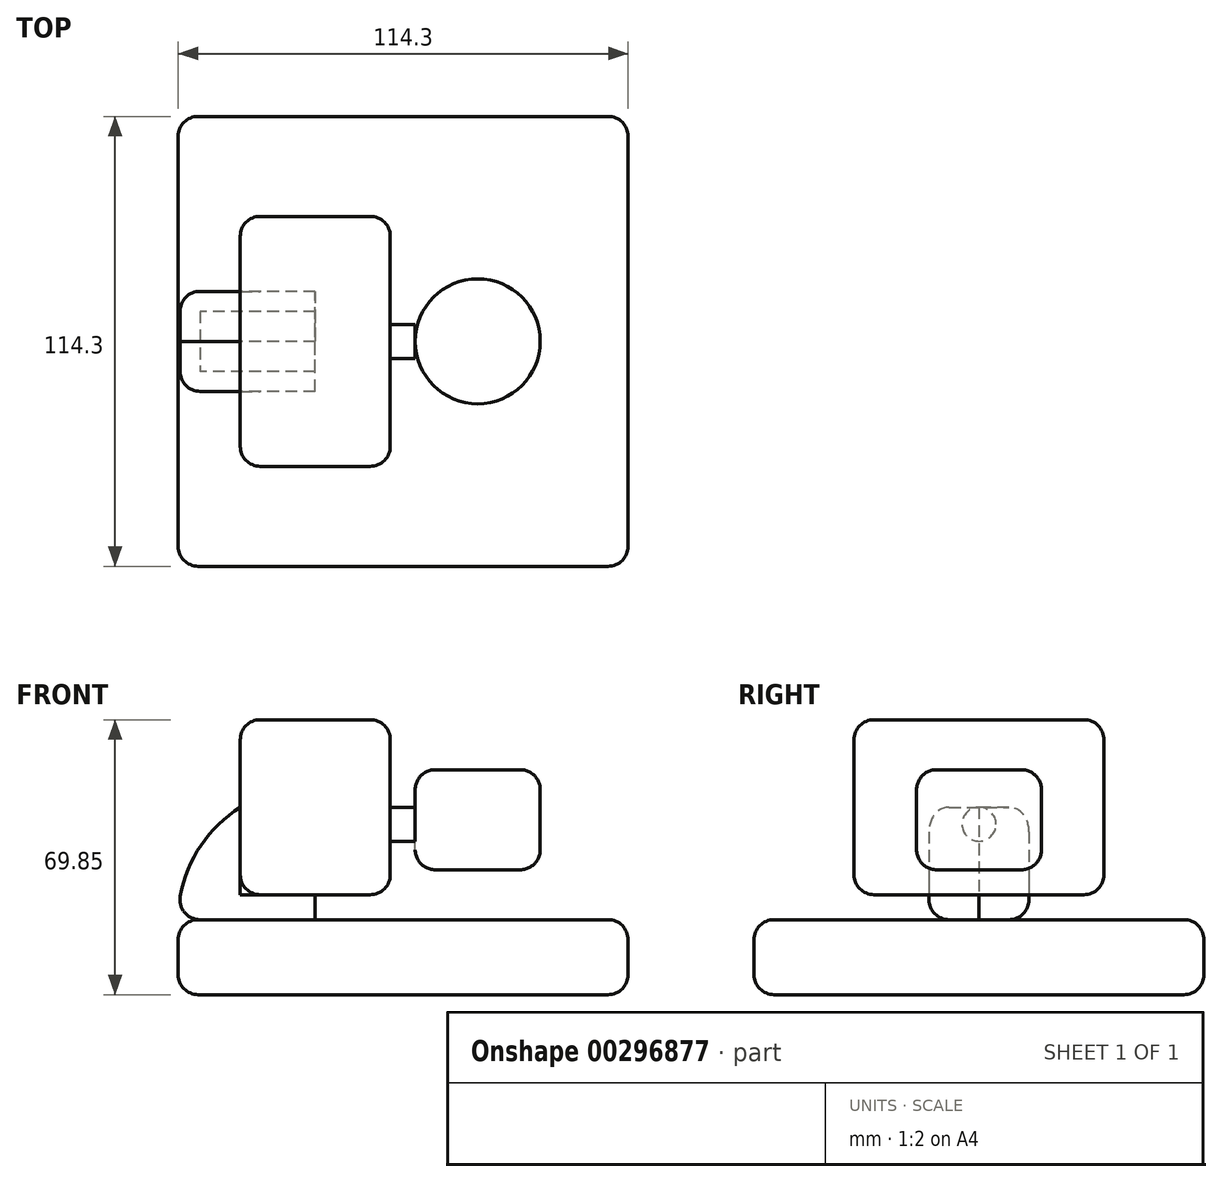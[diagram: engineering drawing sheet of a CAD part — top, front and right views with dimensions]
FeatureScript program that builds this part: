
annotation { "Feature Type Name" : "Feature", "Feature Type Description" : "" }
export const myFeature = defineFeature(function(context is Context, id is Id, definition is map)
    precondition{}
    {
        {
            var Q0;
            Q0=qCreatedBy(makeId("Front.planeOp"),FACE);
            var sketch = newSketch(context, id + "F0", { "sketchPlane" : qUnion([Q0])});
            skLineSegment(sketch, "E0.bottom", {"start": v(57.15, -38.1) * mm, "end": v(-57.15, -38.1) * mm});
            skLineSegment(sketch, "E0.top", {"start": v(57.15, -57.15) * mm, "end": v(-57.15, -57.15) * mm});
            skLineSegment(sketch, "E0.left", {"start": v(57.15, -38.1) * mm, "end": v(57.15, -57.15) * mm});
            skLineSegment(sketch, "E0.right", {"start": v(-57.15, -38.1) * mm, "end": v(-57.15, -57.15) * mm});
            skPoint(sketch, "E0.middle", {"position": v(0, -47.63) * mm});
            skLineSegment(sketch, "E1.bottom", {"start": v(-3.29, 12.7) * mm, "end": v(-41.39, 12.7) * mm});
            skLineSegment(sketch, "E1.top", {"start": v(-3.29, -31.75) * mm, "end": v(-41.39, -31.75) * mm});
            skLineSegment(sketch, "E1.left", {"start": v(-3.29, 12.7) * mm, "end": v(-3.29, -31.75) * mm});
            skLineSegment(sketch, "E1.right", {"start": v(-41.39, 12.7) * mm, "end": v(-41.39, -31.75) * mm});
            skPoint(sketch, "E1.middle", {"position": v(-22.34, -9.53) * mm});
            skLineSegment(sketch, "E2", {"start": v(-22.34, -31.75) * mm, "end": v(-22.34, -38.1) * mm});
            skArc(sketch, "E3", {"start": v(-57.15, -38.1) * mm, "mid": v(-52.95, -21.78) * mm, "end": v(-41.39, -9.53) * mm});
            skLineSegment(sketch, "E4.bottom", {"start": v(34.81, 0) * mm, "end": v(3.06, 0) * mm});
            skLineSegment(sketch, "E4.top", {"start": v(34.81, -25.4) * mm, "end": v(3.06, -25.4) * mm});
            skLineSegment(sketch, "E4.left", {"start": v(34.81, 0) * mm, "end": v(34.81, -25.4) * mm});
            skLineSegment(sketch, "E4.right", {"start": v(3.06, 0) * mm, "end": v(3.06, -25.4) * mm});
            skPoint(sketch, "E4.middle", {"position": v(18.94, -12.7) * mm});
            skLineSegment(sketch, "E5", {"start": v(3.06, -18.16) * mm, "end": v(-3.29, -18.16) * mm});
            skPoint(sketch, "E5.endSnap0", {"position": v(-3.29, -9.53) * mm});
            skLineSegment(sketch, "E6", {"start": v(3.06, -9.53) * mm, "end": v(-3.29, -9.53) * mm});
            skLineSegment(sketch, "E7", {"start": v(18.94, 0) * mm, "end": v(18.94, -25.4) * mm});
            skLineSegment(sketch, "E8", {"start": v(-3.29, -13.84) * mm, "end": v(3.06, -13.84) * mm});
            skSolve(sketch);
        }
        {
            var Q0;
            Q0=makeQuery(id+"F0.imprint","IMPRINT",FACE,{"disambiguationData":[TD([[makeQuery(id+"F0.imprint","IMPRINT",EDGE,{"derivedFrom":sQuery(id+"F0.wireOp",EDGE,"E0.top")}),-1.0]])]});
            extrude(context, id + "F1", {"entities" : qUnion([Q0]), "depth" : 57.15 * mm});
        }
        {
            var Q0;
            Q0=makeQuery(id+"F1.opExtrude","CAP_FACE",FACE,{"disambiguationData":[OSD([sQuery(id+"F0.wireOp",EDGE,"E0.bottom"),sQuery(id+"F0.wireOp",EDGE,"E0.top"),sQuery(id+"F0.wireOp",EDGE,"E0.left"),sQuery(id+"F0.wireOp",EDGE,"E0.right")])],"isStart":true});
            extrude(context, id + "F2", {"entities" : qUnion([Q0]), "operationType" : NewBodyOperationType.ADD, "depth" : 57.15 * mm});
        }
        {
            var Q0;
            {var subQ1=sQuery(id+"F0.wireOp",EDGE,"E1.bottom");Q0=makeQuery(id+"F0.imprint","IMPRINT",FACE,{"disambiguationData":[TD([[makeQuery(id+"F0.imprint","IMPRINT",EDGE,{"derivedFrom":subQ1}),1.0]])]});}
            extrude(context, id + "F3", {"entities" : qUnion([Q0]), "depth" : 31.75 * mm});
        }
        {
            var Q0;
            {var subQ1=sQuery(id+"F0.wireOp",EDGE,"E1.bottom");Q0=makeQuery(id+"F0.imprint","IMPRINT",FACE,{"disambiguationData":[TD([[makeQuery(id+"F0.imprint","IMPRINT",EDGE,{"derivedFrom":subQ1}),1.0]])]});}
            extrude(context, id + "F4", {"entities" : qUnion([Q0]), "operationType" : NewBodyOperationType.ADD, "oppositeDirection" : true, "depth" : 31.75 * mm});
        }
        {
            var Q0;
            {var subQ0=sQuery(id+"F0.wireOp",EDGE,"E4.left");Q0=makeQuery(id+"F0.imprint","IMPRINT",FACE,{"disambiguationData":[TD([[makeQuery(id+"F0.imprint","IMPRINT",EDGE,{"derivedFrom":subQ0}),-1.0]])]});}
            var Q1;
            Q1=sQuery(id+"F0.wireOp",EDGE,"E7");
            revolve(context, id + "F5", {"entities" : qUnion([Q0]), "axis" : qUnion([Q1]), "revolveType" : RevolveType.FULL});
        }
        {
            var Q0;
            {var subQ0=sQuery(id+"F0.wireOp",EDGE,"E2");Q0=makeQuery(id+"F0.imprint","IMPRINT",FACE,{"disambiguationData":[TD([[makeQuery(id+"F0.imprint","IMPRINT",EDGE,{"derivedFrom":subQ0}),-1.0]])]});}
            extrude(context, id + "F6", {"entities" : qUnion([Q0]), "depth" : 12.7 * mm});
        }
        {
            var Q0;
            {var subQ0=sQuery(id+"F0.wireOp",EDGE,"E2");Q0=makeQuery(id+"F0.imprint","IMPRINT",FACE,{"disambiguationData":[TD([[makeQuery(id+"F0.imprint","IMPRINT",EDGE,{"derivedFrom":subQ0}),-1.0]])]});}
            extrude(context, id + "F7", {"entities" : qUnion([Q0]), "oppositeDirection" : true, "depth" : 12.7 * mm});
        }
        {
            var Q0;
            {var subQ0=sQuery(id+"F0.wireOp",EDGE,"E5");Q0=makeQuery(id+"F0.imprint","IMPRINT",FACE,{"disambiguationData":[TD([[makeQuery(id+"F0.imprint","IMPRINT",EDGE,{"derivedFrom":subQ0}),-1.0]])]});}
            var Q1;
            Q1=sQuery(id+"F0.wireOp",EDGE,"E8");
            revolve(context, id + "F8", {"entities" : qUnion([Q0]), "axis" : qUnion([Q1]), "revolveType" : RevolveType.FULL});
        }
        {
            var Q0;
            Q0=makeQuery(id+"F1.opExtrude","CAP_EDGE",EDGE,{"disambiguationData":[OSD([sQuery(id+"F0.wireOp",EDGE,"E0.bottom")])],"isStart":false});
            fillet(context, id + "F9", {"entities" : qUnion([Q0]), "radius" : 5.08 * mm, "tangentPropagation" : true, "allowEdgeOverflow" : false});
        }
        {
            var Q0;
            Q0=makeQuery(id+"F1.opExtrude","CAP_EDGE",EDGE,{"disambiguationData":[OSD([sQuery(id+"F0.wireOp",EDGE,"E0.right")])],"isStart":false});
            fillet(context, id + "F10", {"entities" : qUnion([Q0]), "radius" : 5.08 * mm, "tangentPropagation" : true, "allowEdgeOverflow" : false});
        }
        {
            var Q0;
            Q0=makeQuery(id+"F1.opExtrude","CAP_EDGE",EDGE,{"disambiguationData":[OSD([sQuery(id+"F0.wireOp",EDGE,"E0.top")])],"isStart":false});
            fillet(context, id + "F11", {"entities" : qUnion([Q0]), "radius" : 5.08 * mm, "tangentPropagation" : true, "allowEdgeOverflow" : false});
        }
        {
            var Q0;
            Q0=makeQuery(id+"F1.opExtrude","CAP_EDGE",EDGE,{"disambiguationData":[OSD([sQuery(id+"F0.wireOp",EDGE,"E0.left")])],"isStart":false});
            fillet(context, id + "F12", {"entities" : qUnion([Q0]), "radius" : 5.08 * mm, "tangentPropagation" : true, "allowEdgeOverflow" : false});
        }
        {
            var Q0;
            Q0=makeQuery(id+"F6.opExtrude","SWEPT_EDGE",EDGE,{"disambiguationData":[OSD([sQuery(id+"F0.wireOp",EDGE,"E0.bottom"),sQuery(id+"F0.wireOp",EDGE,"E0.right"),sQuery(id+"F0.wireOp",EDGE,"E3")])]});
            var Q1;
            Q1=makeQuery(id+"F7.opExtrude","SWEPT_EDGE",EDGE,{"disambiguationData":[OSD([sQuery(id+"F0.wireOp",EDGE,"E0.bottom"),sQuery(id+"F0.wireOp",EDGE,"E0.right"),sQuery(id+"F0.wireOp",EDGE,"E3")])]});
            fillet(context, id + "F13", {"entities" : qUnion([Q0, Q1]), "radius" : 5.08 * mm, "tangentPropagation" : true, "allowEdgeOverflow" : false});
        }
        {
            var Q0;
            Q0=makeQuery(id+"F2.opExtrude","CAP_EDGE",EDGE,{"disambiguationData":[OSD([sQuery(id+"F0.wireOp",EDGE,"E0.bottom")])],"isStart":false});
            fillet(context, id + "F14", {"entities" : qUnion([Q0]), "radius" : 5.08 * mm, "tangentPropagation" : true, "allowEdgeOverflow" : false});
        }
        {
            var Q0;
            Q0=makeQuery(id+"F6.opExtrude","CAP_EDGE",EDGE,{"disambiguationData":[OSD([sQuery(id+"F0.wireOp",EDGE,"E3")])],"isStart":false});
            var Q1;
            Q1=makeQuery(id+"F7.opExtrude","CAP_EDGE",EDGE,{"disambiguationData":[OSD([sQuery(id+"F0.wireOp",EDGE,"E3")])],"isStart":false});
            fillet(context, id + "F15", {"entities" : qUnion([Q0, Q1]), "radius" : 5.08 * mm, "tangentPropagation" : true, "allowEdgeOverflow" : false});
        }
        {
            var Q0;
            Q0=makeQuery(id+"F3.opExtrude","CAP_EDGE",EDGE,{"disambiguationData":[OSD([sQuery(id+"F0.wireOp",EDGE,"E1.right")])],"isStart":false});
            var Q1;
            Q1=makeQuery(id+"F3.opExtrude","CAP_EDGE",EDGE,{"disambiguationData":[OSD([sQuery(id+"F0.wireOp",EDGE,"E1.bottom")])],"isStart":false});
            var Q2;
            Q2=makeQuery(id+"F3.opExtrude","CAP_EDGE",EDGE,{"disambiguationData":[OSD([sQuery(id+"F0.wireOp",EDGE,"E1.left")])],"isStart":false});
            var Q3;
            Q3=makeQuery(id+"F3.opExtrude","CAP_EDGE",EDGE,{"disambiguationData":[OSD([sQuery(id+"F0.wireOp",EDGE,"E1.top")])],"isStart":false});
            fillet(context, id + "F16", {"entities" : qUnion([Q0, Q1, Q2, Q3]), "radius" : 5.08 * mm, "tangentPropagation" : true, "allowEdgeOverflow" : false});
        }
        {
            var Q0;
            Q0=makeQuery(id+"F5.opRevolve","SWEPT_EDGE",EDGE,{"disambiguationData":[OSD([sQuery(id+"F0.wireOp",EDGE,"E4.bottom"),sQuery(id+"F0.wireOp",EDGE,"E4.left")])]});
            fillet(context, id + "F17", {"entities" : qUnion([Q0]), "radius" : 5.08 * mm, "tangentPropagation" : true, "allowEdgeOverflow" : false});
        }
        {
            var Q0;
            Q0=makeQuery(id+"F5.opRevolve","SWEPT_EDGE",EDGE,{"disambiguationData":[OSD([sQuery(id+"F0.wireOp",EDGE,"E4.top"),sQuery(id+"F0.wireOp",EDGE,"E4.left")])]});
            fillet(context, id + "F18", {"entities" : qUnion([Q0]), "radius" : 5.08 * mm, "tangentPropagation" : true, "allowEdgeOverflow" : false});
        }
        {
            var Q0;
            Q0=makeQuery(id+"F4.opExtrude","CAP_EDGE",EDGE,{"disambiguationData":[OSD([sQuery(id+"F0.wireOp",EDGE,"E1.bottom")])],"isStart":false});
            var Q1;
            Q1=makeQuery(id+"F4.opExtrude","CAP_EDGE",EDGE,{"disambiguationData":[OSD([sQuery(id+"F0.wireOp",EDGE,"E1.right")])],"isStart":false});
            var Q2;
            Q2=makeQuery(id+"F4.opExtrude","CAP_EDGE",EDGE,{"disambiguationData":[OSD([sQuery(id+"F0.wireOp",EDGE,"E1.top")])],"isStart":false});
            var Q3;
            Q3=makeQuery(id+"F4.opExtrude","CAP_EDGE",EDGE,{"disambiguationData":[OSD([sQuery(id+"F0.wireOp",EDGE,"E1.left")])],"isStart":false});
            fillet(context, id + "F19", {"entities" : qUnion([Q0, Q1, Q2, Q3]), "radius" : 5.08 * mm, "tangentPropagation" : true, "allowEdgeOverflow" : false});
        }
        {
            var Q0;
            {var subQ0=sQuery(id+"F0.wireOp",EDGE,"E1.left");var subQ1=sQuery(id+"F0.wireOp",EDGE,"E1.bottom");Q0=makeQuery(id+"F4.boolean.opBoolean","MERGE",EDGE,{"derivedFrom":[makeQuery(id+"F3.opExtrude","SWEPT_EDGE",EDGE,{"disambiguationData":[OSD([subQ1,subQ0])]}),makeQuery(id+"F4.opExtrude","SWEPT_EDGE",EDGE,{"disambiguationData":[OSD([subQ1,subQ0])]})]});}
            var Q1;
            {var subQ0=sQuery(id+"F0.wireOp",EDGE,"E1.right");var subQ1=sQuery(id+"F0.wireOp",EDGE,"E1.bottom");Q1=makeQuery(id+"F4.boolean.opBoolean","MERGE",EDGE,{"derivedFrom":[makeQuery(id+"F3.opExtrude","SWEPT_EDGE",EDGE,{"disambiguationData":[OSD([subQ1,subQ0])]}),makeQuery(id+"F4.opExtrude","SWEPT_EDGE",EDGE,{"disambiguationData":[OSD([subQ1,subQ0])]})]});}
            fillet(context, id + "F20", {"entities" : qUnion([Q0, Q1]), "radius" : 5.08 * mm, "tangentPropagation" : true, "allowEdgeOverflow" : false});
        }
        {
            var Q0;
            {var subQ0=sQuery(id+"F0.wireOp",EDGE,"E1.left");var subQ1=sQuery(id+"F0.wireOp",EDGE,"E1.top");Q0=makeQuery(id+"F4.boolean.opBoolean","MERGE",EDGE,{"derivedFrom":[makeQuery(id+"F3.opExtrude","SWEPT_EDGE",EDGE,{"disambiguationData":[OSD([subQ1,subQ0])]}),makeQuery(id+"F4.opExtrude","SWEPT_EDGE",EDGE,{"disambiguationData":[OSD([subQ1,subQ0])]})]});}
            var Q1;
            {var subQ0=sQuery(id+"F0.wireOp",EDGE,"E1.right");var subQ1=sQuery(id+"F0.wireOp",EDGE,"E1.top");Q1=makeQuery(id+"F4.boolean.opBoolean","MERGE",EDGE,{"derivedFrom":[makeQuery(id+"F3.opExtrude","SWEPT_EDGE",EDGE,{"disambiguationData":[OSD([subQ1,subQ0])]}),makeQuery(id+"F4.opExtrude","SWEPT_EDGE",EDGE,{"disambiguationData":[OSD([subQ1,subQ0])]})]});}
            fillet(context, id + "F21", {"entities" : qUnion([Q0, Q1]), "radius" : 5.08 * mm, "tangentPropagation" : true, "allowEdgeOverflow" : false});
        }
    });
